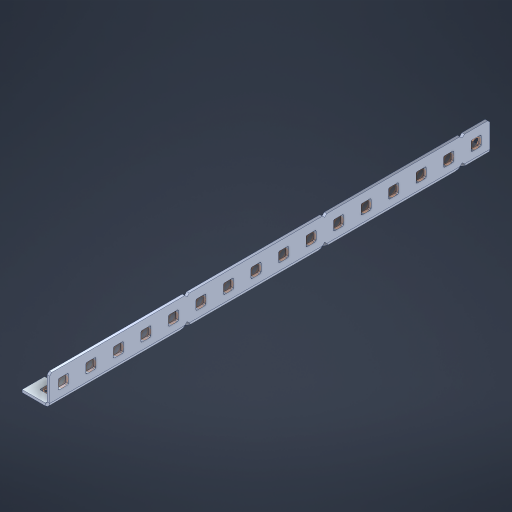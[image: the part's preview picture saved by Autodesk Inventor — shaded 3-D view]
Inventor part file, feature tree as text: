
AUTODESK INVENTOR PART (.ipt)
format: ipt  version: 2023 (Build 270158000, 158)  size: 837,632 bytes
history: native  units: in
note: dims shown in document units (in); Inventor stores cm internally (conversion verified against a paired STEP export)
features: other x55, extrude x46, sheet_metal_op x11, sketch x10, pattern_linear x2, mirror x1, chamfer x1
ambient origin geometry x8: Origin, YZ Plane, XZ Plane, XY Plane, X Axis, Y Axis, Z Axis, Center Point
bodies: Solid1 (feature_tree), Body (feature_tree)
feature tree (126):
  sheet_metal_op  "Flanges"
  other  "Flange Pattern Plane"
  other  "Flange Pattern Sketch"
  sheet_metal_op  "Flange Pattern"
  sheet_metal_op  "Body Pattern"
  pattern_linear  "Center Pattern"  Spacing1=0.0469in  [1 undecoded]
  other  "Arc Length"
  mirror  "Notch Mirror"
  pattern_linear  "Notch Pattern"  Spacing1=0.182in  [1 undecoded]
  chamfer  "End Chamfer"
  extrude  "Half Cut"  Depth=0.02in
  sketch  "Sketch1"  dims[d0=1.0in]
  other  "Plate1"
  sketch  "Sketch2"  dims[d1=8.0in]
  other  "Plate2"
  sheet_metal_op  "Bend1"
  sheet_metal_op  "Corner1"
  sketch  "Sketch3"  dims[d2=0.0469in]
  sketch  "Sketch7"  dims[d3=0.0469in]
  other  "Srf1"
  other  "Srf2"
  sketch  "Sketch8"  dims[d4=0.0234in]
  sketch  "Sketch9"  dims[d5=0.0938in]
  other  "Srf91"
  sheet_metal_op  "Body Pattern Sketch"
  other  "Srf92"
  sketch  "Sketch13"  dims[d6=0.0469in]
  sketch  "Sketch14"  dims[d7=0.5in d8=90.0deg d9=0.0312in]
  sketch  "Sketch15"  dims[d10=0.1875in]
  sketch  "Sketch16"  dims[d11=0.0469in d12=0.0469in d16=0.182in d17=0.02in d18=0.0469in d19=0.0in d20=0.25in d21=0.25in d38=6.2992in d40=0.5in d41=0.3937in d43=1.0in d46=0.172in d47=1.0in d48=0.0in d49=0.182in d50=0.02in d51=0.25in d52=0.25in d53=0.0469in d54=0.0in d55=0.172in d56=1.0in d57=0.0in d58=0.25in d60=6.2992in d62=0.5in d63=0.3937in d65=0.5in d85=0.1227in d86=0.1659in d88=0.04in d89=0.0469in d90=0.0in d91=0.04in d92=0.0491in d95=2.5in d96=0.04in d97=0.25in d98=45.0deg d99=0.25in d100=0.5in d101=0.0in d102=2.497in d106=0.182in d107=0.02in d108=0.5in d109=0.5in d110=0.0469in d111=0.0in d112=0.172in d113=0.5in d114=0.0in d117=0.5in d118=0.5in d119=0.5in]
  other  "Srf786"
  other  "Srf823"
  other  "Srf824"
  other  "Srf825"
  other  "Srf826"
  other  "Srf827"
  other  "Srf828"
  other  "Srf829"
  other  "Srf856"
  other  "Srf857"
  other  "Srf858"
  other  "Srf859"
  other  "Srf860"
  other  "Srf861"
  other  "Srf862"
  other  "Srf889"
  other  "Srf890"
  other  "Srf891"
  other  "Srf892"
  other  "Srf893"
  other  "Srf894"
  other  "Srf895"
  other  "Srf896"
  other  "Srf922"
  other  "Srf923"
  other  "Srf924"
  other  "Srf925"
  other  "Srf926"
  other  "Srf959"
  other  "Srf960"
  other  "Srf961"
  other  "Srf962"
  other  "Srf963"
  other  "Srf996"
  other  "Srf997"
  other  "Srf998"
  other  "Srf999"
  other  "Srf1000"
  other  "Srf1143"
  other  "Srf1144"
  other  "Srf1199"
  other  "Srf1200"
  other  "Srf1255"
  other  "Srf1256"
  sheet_metal_op  "Flange Stamp"
  sheet_metal_op  "Flange Circle"
  sheet_metal_op  "Body Stamp"
  sheet_metal_op  "Body Circle"
  other  "Center Stamp"
  other  "Center Circle"
  sheet_metal_op  "Notch"
  extrude  "ExtrusionSrf2"  Depth=0.0469in
  extrude  "ExtrusionSrf92"  TaperAngle=0.0deg  [1 undecoded]
  extrude  "ExtrusionSrf823"  Depth=0.25in
  extrude  "ExtrusionSrf824"  Depth=0.25in
  extrude  "ExtrusionSrf825"  Depth=0.5in
  extrude  "ExtrusionSrf826"  Depth=0.5in
  extrude  "ExtrusionSrf827"  Depth=1.0in TaperAngle=0.0deg
  extrude  "ExtrusionSrf828"  Depth=0.182in
  extrude  "ExtrusionSrf829"  Depth=0.02in
  extrude  "ExtrusionSrf856"  Depth=0.25in
  extrude  "ExtrusionSrf857"  Depth=0.25in
  extrude  "ExtrusionSrf858"  Depth=0.0469in
  extrude  "ExtrusionSrf859"  TaperAngle=0.0deg  [1 undecoded]
  extrude  "ExtrusionSrf860"  Depth=0.5in
  extrude  "ExtrusionSrf861"  Depth=1.0in TaperAngle=0.0deg
  extrude  "ExtrusionSrf862"  Depth=0.25in
  extrude  "ExtrusionSrf889"  Depth=0.5in
  extrude  "ExtrusionSrf890"  Depth=0.5in
  extrude  "ExtrusionSrf891"  Depth=0.5in
  extrude  "ExtrusionSrf892"  Depth=0.5in
  extrude  "ExtrusionSrf893"  Depth=0.5in
  extrude  "ExtrusionSrf894"  Depth=0.0469in
  extrude  "ExtrusionSrf895"  TaperAngle=0.0deg  [1 undecoded]
  extrude  "ExtrusionSrf896"  Depth=0.5in
  extrude  "ExtrusionSrf922"  Depth=0.5in
  extrude  "ExtrusionSrf923"  Depth=2.5in
  extrude  "ExtrusionSrf924"  Depth=0.25in TaperAngle=45.0deg
  extrude  "ExtrusionSrf925"  Depth=0.25in
  extrude  "ExtrusionSrf926"  Depth=0.5in TaperAngle=0.0deg
  extrude  "ExtrusionSrf959"  Depth=0.5in
  extrude  "ExtrusionSrf960"  Depth=0.182in
  extrude  "ExtrusionSrf961"  Depth=0.02in
  extrude  "ExtrusionSrf962"  Depth=0.5in
  extrude  "ExtrusionSrf963"  Depth=0.5in
  extrude  "ExtrusionSrf996"  Depth=0.0469in
  extrude  "ExtrusionSrf997"  TaperAngle=0.0deg  [1 undecoded]
  extrude  "ExtrusionSrf998"  Depth=0.5in
  extrude  "ExtrusionSrf999"  Depth=0.5in TaperAngle=0.0deg
  extrude  "ExtrusionSrf1000"  Depth=0.5in
  extrude  "ExtrusionSrf1143"  Depth=0.5in
  extrude  "ExtrusionSrf1144"  Depth=0.5in
  extrude  "ExtrusionSrf1199"  [1 undecoded]
  extrude  "ExtrusionSrf1200"  [1 undecoded]
  extrude  "ExtrusionSrf1255"  [1 undecoded]
  extrude  "ExtrusionSrf1256"  [1 undecoded]
note: 10 required parameter values undecoded (feature->parameter linkage not recoverable at this tier; creation-order binding heuristic only, values carry confidence <= 0.55)
